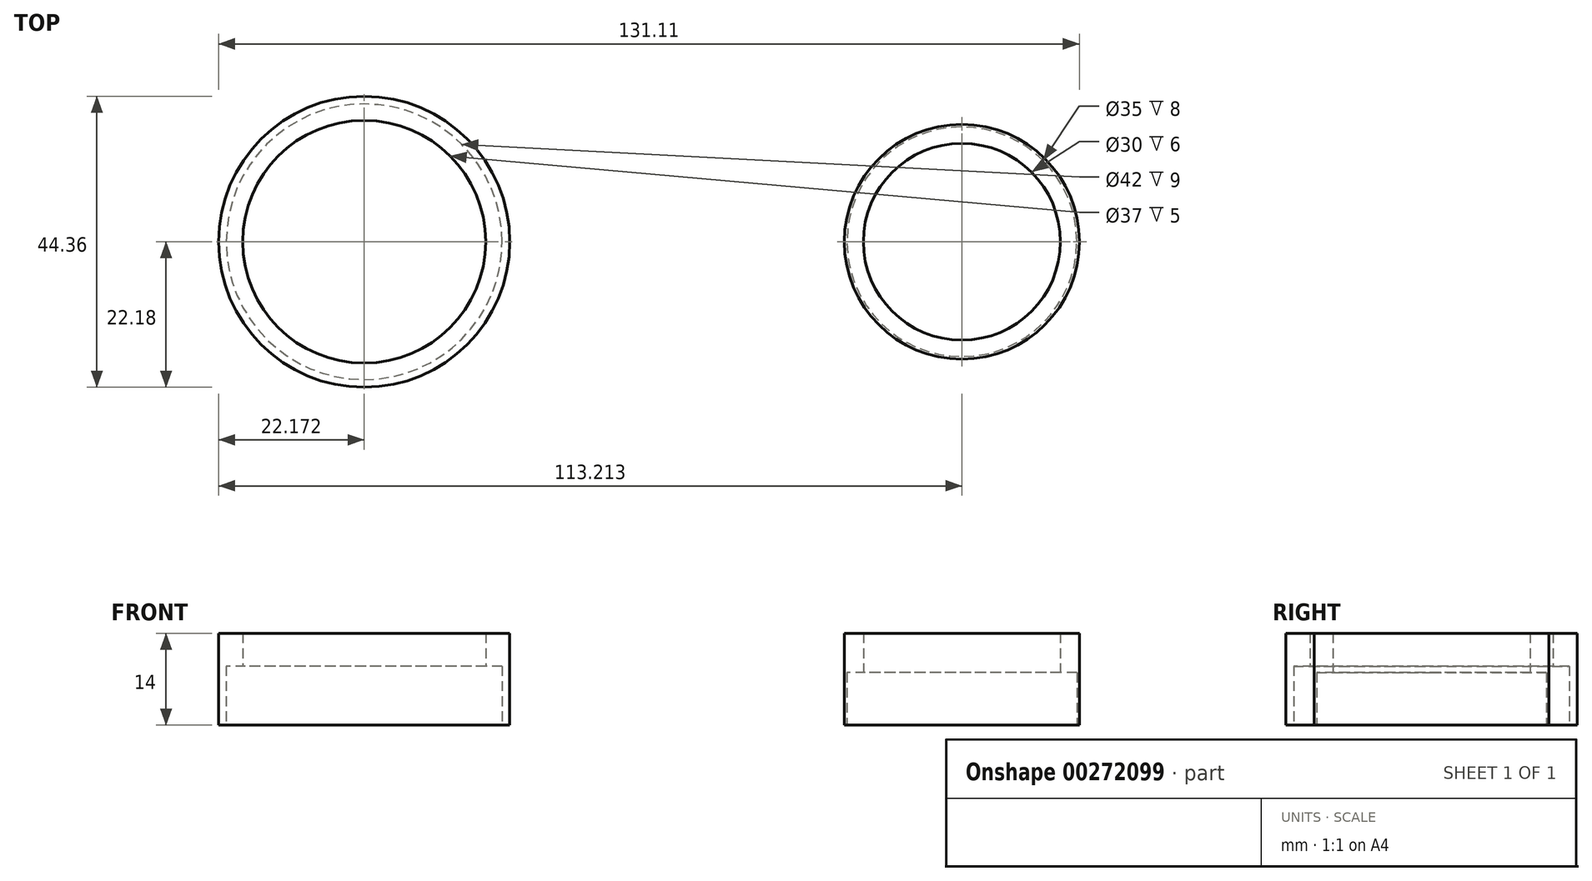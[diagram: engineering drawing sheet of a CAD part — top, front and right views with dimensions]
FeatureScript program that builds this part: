
annotation { "Feature Type Name" : "Feature", "Feature Type Description" : "" }
export const myFeature = defineFeature(function(context is Context, id is Id, definition is map)
    precondition{}
    {
        {
            var Q0;
            Q0=qCreatedBy(makeId("Top.planeOp"),FACE);
            var sketch = newSketch(context, id + "F0", { "sketchPlane" : qUnion([Q0])});
            skCircle(sketch, "E0", {"center": v(-47.02, 0) * mm, "radius": 22.18 * mm});
            skCircle(sketch, "E1", {"center": v(44.02, 0) * mm, "radius": 17.9 * mm});
            skCircle(sketch, "E2", {"center": v(-47.02, 0) * mm, "radius": 21 * mm});
            skCircle(sketch, "E3", {"center": v(44.02, 0) * mm, "radius": 17.5 * mm});
            skSolve(sketch);
        }
        {
            var Q0;
            Q0=makeQuery(id+"F0.imprint","IMPRINT",FACE,{"disambiguationData":[TD([[makeQuery(id+"F0.imprint","IMPRINT",EDGE,{"derivedFrom":sQuery(id+"F0.wireOp",EDGE,"E0")}),1.0]])]});
            extrude(context, id + "F1", {"entities" : qUnion([Q0]), "depth" : 9 * mm});
        }
        {
            var Q0;
            Q0=makeQuery(id+"F0.imprint","IMPRINT",FACE,{"disambiguationData":[TD([[makeQuery(id+"F0.imprint","IMPRINT",EDGE,{"derivedFrom":sQuery(id+"F0.wireOp",EDGE,"E1")}),1.0]])]});
            extrude(context, id + "F2", {"entities" : qUnion([Q0]), "depth" : 8 * mm});
        }
        {
            var Q0;
            Q0=makeQuery(id+"F1.opExtrude","CAP_FACE",FACE,{"disambiguationData":[OSD([sQuery(id+"F0.wireOp",EDGE,"E0"),sQuery(id+"F0.wireOp",EDGE,"E2")])],"isStart":false});
            var sketch = newSketch(context, id + "F3", { "sketchPlane" : qUnion([Q0])});
            skCircle(sketch, "E4.0", {"center": v(-47.02, 0) * mm, "radius": 22.18 * mm});
            skCircle(sketch, "E5.0", {"center": v(-47.02, 0) * mm, "radius": 18.5 * mm});
            skSolve(sketch);
        }
        {
            var Q0;
            Q0=makeQuery(id+"F3.imprint","IMPRINT",FACE,{"disambiguationData":[TD([[makeQuery(id+"F3.imprint","IMPRINT",EDGE,{"derivedFrom":sQuery(id+"F3.wireOp",EDGE,"E5.0")}),-1.0]])]});
            var Q1;
            Q1=makeQuery(id+"F3.imprint","IMPRINT",FACE,{"disambiguationData":[TD([[makeQuery(id+"F3.imprint","IMPRINT",EDGE,{"derivedFrom":sQuery(id+"F3.wireOp",EDGE,"E4.0")}),1.0]])]});
            extrude(context, id + "F4", {"entities" : qUnion([Q0, Q1]), "operationType" : NewBodyOperationType.ADD, "depth" : 5 * mm});
        }
        {
            var Q0;
            Q0=makeQuery(id+"F2.opExtrude","CAP_FACE",FACE,{"disambiguationData":[OSD([sQuery(id+"F0.wireOp",EDGE,"E1"),sQuery(id+"F0.wireOp",EDGE,"E3")])],"isStart":false});
            var sketch = newSketch(context, id + "F5", { "sketchPlane" : qUnion([Q0])});
            skCircle(sketch, "E6.0", {"center": v(44.02, 0) * mm, "radius": 17.9 * mm});
            skCircle(sketch, "E7.0", {"center": v(44.02, 0) * mm, "radius": 15 * mm});
            skSolve(sketch);
        }
        {
            var Q0;
            Q0 = qSketchRegion(id + "F5", true);
            extrude(context, id + "F6", {"entities" : qUnion([Q0]), "operationType" : NewBodyOperationType.ADD, "depth" : 6 * mm});
        }
    });
